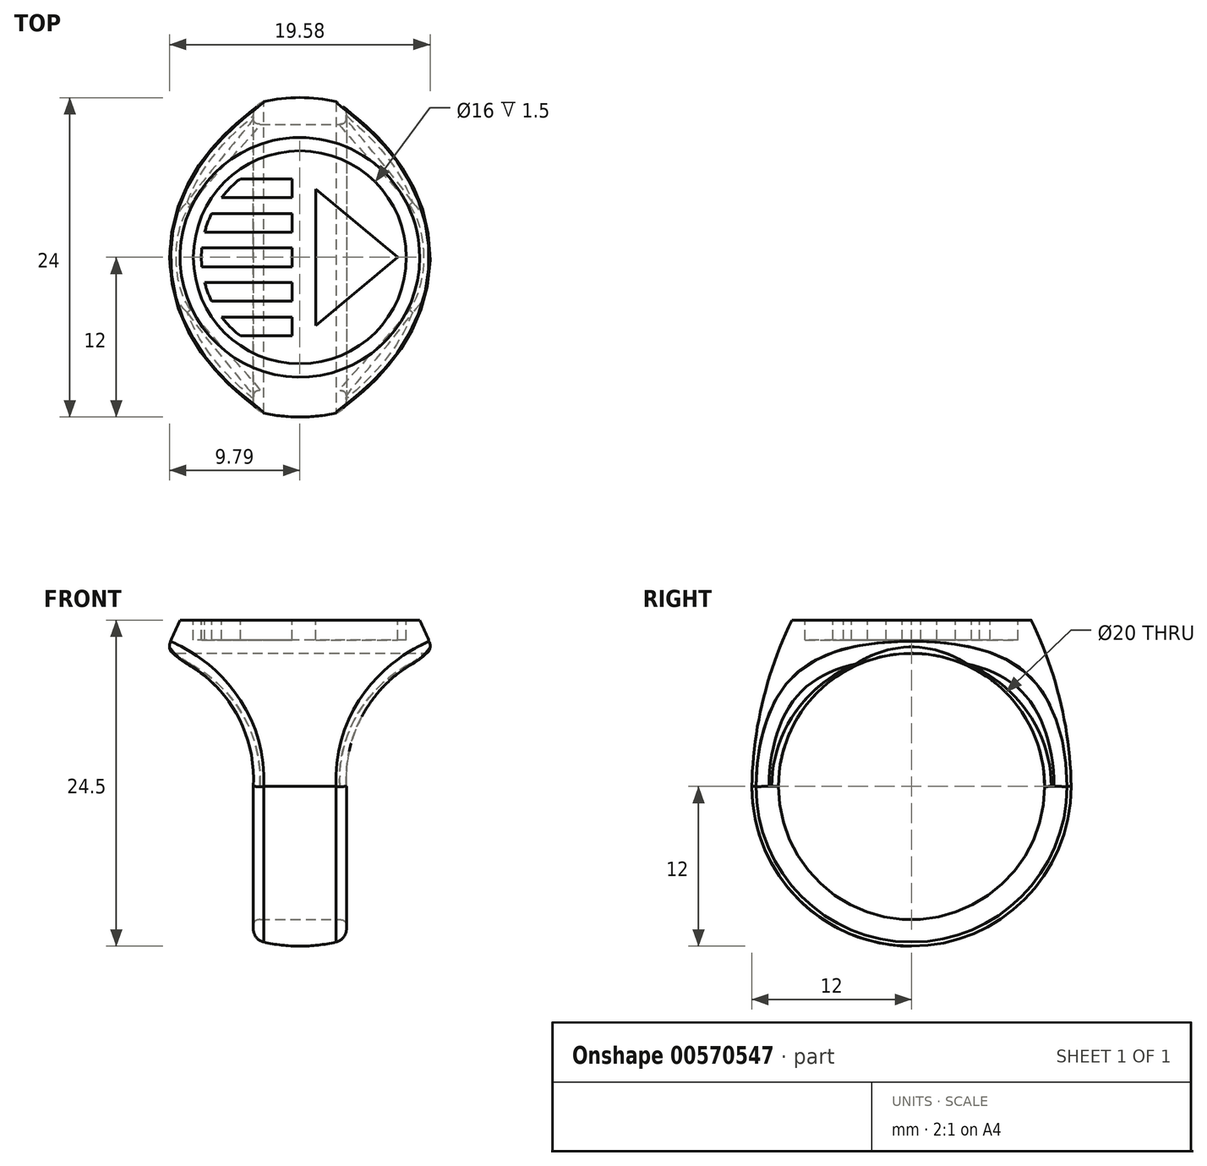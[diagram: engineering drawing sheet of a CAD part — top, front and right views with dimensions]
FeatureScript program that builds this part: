
annotation { "Feature Type Name" : "Feature", "Feature Type Description" : "" }
export const myFeature = defineFeature(function(context is Context, id is Id, definition is map)
    precondition{}
    {
        {
            var Q0;
            Q0=qCreatedBy(makeId("Right.planeOp"),FACE);
            var sketch = newSketch(context, id + "F0", { "sketchPlane" : qUnion([Q0])});
            skLineSegment(sketch, "E0", {"start": v(0, 0) * mm, "end": v(0, -24.5) * mm});
            skLineSegment(sketch, "E1", {"start": v(0, 0) * mm, "end": v(-9, 0) * mm});
            skArc(sketch, "E2", {"start": v(-12, -12.5) * mm, "mid": v(-8.49, -20.99) * mm, "end": v(0, -24.5) * mm});
            skLineSegment(sketch, "E3", {"start": v(0, -12.5) * mm, "end": v(-12, -12.5) * mm, "construction": true});
            skArc(sketch, "E4", {"start": v(-9, 0) * mm, "mid": v(-11.18, -6.09) * mm, "end": v(-12, -12.5) * mm});
            skSolve(sketch);
        }
        {
            var Q0;
            Q0=makeQuery(id+"F0.imprint","IMPRINT",FACE,{"disambiguationData":[TD([[makeQuery(id+"F0.imprint","IMPRINT",EDGE,{"derivedFrom":sQuery(id+"F0.wireOp",EDGE,"E0")}),-1.0]])]});
            var Q1;
            Q1=sQuery(id+"F0.wireOp",EDGE,"E0");
            revolve(context, id + "F1", {"entities" : qUnion([Q0]), "axis" : qUnion([Q1]), "revolveType" : RevolveType.FULL});
        }
        {
            var Q0;
            Q0=qCreatedBy(makeId("Right.planeOp"),FACE);
            var sketch = newSketch(context, id + "F2", { "sketchPlane" : qUnion([Q0])});
            skCircle(sketch, "E5", {"center": v(0, -12.5) * mm, "radius": 10 * mm});
            skSolve(sketch);
        }
        {
            var Q0;
            Q0=qSketchRegion(id+"F2",true);
            extrude(context, id + "F3", {"entities" : qUnion([Q0]), "operationType" : NewBodyOperationType.REMOVE, "oppositeDirection" : true, "depth" : 25 * mm, "offsetDistance" : 25 * mm, "symmetric" : true});
        }
        {
            var Q0;
            Q0=qCreatedBy(makeId("Front.planeOp"),FACE);
            var sketch = newSketch(context, id + "F4", { "sketchPlane" : qUnion([Q0])});
            skLineSegment(sketch, "E6", {"start": v(3.5, -26.5) * mm, "end": v(3.5, -12.5) * mm});
            skArc(sketch, "E7", {"start": v(10.15, -2.5) * mm, "mid": v(5.16, -6.39) * mm, "end": v(3.5, -12.5) * mm});
            skLineSegment(sketch, "E8", {"start": v(10.15, -2.5) * mm, "end": v(11.65, -2.5) * mm});
            skLineSegment(sketch, "E9", {"start": v(11.65, -2.5) * mm, "end": v(11.65, -26.5) * mm});
            skLineSegment(sketch, "E10", {"start": v(11.65, -26.5) * mm, "end": v(3.5, -26.5) * mm});
            skPoint(sketch, "E11.start.orphan", {"position": v(0, -24.5) * mm});
            skLineSegment(sketch, "E12", {"start": v(0, 0) * mm, "end": v(0, -24.5) * mm, "construction": true});
            skLineSegment(sketch, "E13.MirrorCS", {"start": v(-3.5, -26.5) * mm, "end": v(-3.5, -12.5) * mm});
            skArc(sketch, "E14.MirrorCS", {"start": v(-10.15, -2.5) * mm, "mid": v(-5.16, -6.39) * mm, "end": v(-3.5, -12.5) * mm});
            skLineSegment(sketch, "E15.MirrorCS", {"start": v(-11.65, -2.5) * mm, "end": v(-11.65, -26.5) * mm});
            skLineSegment(sketch, "E16.MirrorCS", {"start": v(-11.65, -26.5) * mm, "end": v(-3.5, -26.5) * mm});
            skLineSegment(sketch, "E17.MirrorCS", {"start": v(-10.15, -2.5) * mm, "end": v(-11.65, -2.5) * mm});
            skSolve(sketch);
        }
        {
            var Q0;
            Q0=qSketchRegion(id+"F4",true);
            extrude(context, id + "F5", {"entities" : qUnion([Q0]), "operationType" : NewBodyOperationType.REMOVE, "depth" : 25 * mm, "offsetDistance" : 25 * mm, "symmetric" : true});
        }
        {
            var Q0;
            Q0=makeQuery(id+"F1.opRevolve","SWEPT_FACE",FACE,{"disambiguationData":[OSD([sQuery(id+"F0.wireOp",EDGE,"E1")])]});
            var sketch = newSketch(context, id + "F6", { "sketchPlane" : qUnion([Q0])});
            skCircle(sketch, "E18", {"center": v(0, 0) * mm, "radius": 8 * mm});
            skLineSegment(sketch, "E19", {"start": v(-8, 0) * mm, "end": v(8, 0) * mm, "construction": true});
            skLineSegment(sketch, "E20", {"start": v(0, 7.69) * mm, "end": v(7.93, 1.07) * mm});
            skLineSegment(sketch, "E21", {"start": v(1.2, 0) * mm, "end": v(1.2, 5.13) * mm});
            skLineSegment(sketch, "E22", {"start": v(1.2, 5.13) * mm, "end": v(7.34, 0) * mm});
            skLineSegment(sketch, "E23", {"start": v(0, 7.69) * mm, "end": v(0, 0) * mm});
            skArc(sketch, "E24.trimOffspring", {"start": v(-4.47, 5.9) * mm, "mid": v(-5.22, 5.25) * mm, "end": v(-5.88, 4.5) * mm});
            skLineSegment(sketch, "E25", {"start": v(-7.37, 0.7) * mm, "end": v(-0.6, 0.7) * mm});
            skLineSegment(sketch, "E26", {"start": v(-0.6, 0.7) * mm, "end": v(-0.6, 0) * mm});
            skLineSegment(sketch, "E27", {"start": v(-7.15, 1.9) * mm, "end": v(-0.6, 1.9) * mm});
            skLineSegment(sketch, "E28", {"start": v(-0.6, 1.9) * mm, "end": v(-0.6, 3.3) * mm});
            skLineSegment(sketch, "E29", {"start": v(-0.6, 3.3) * mm, "end": v(-6.62, 3.3) * mm});
            skLineSegment(sketch, "E30", {"start": v(-5.88, 4.5) * mm, "end": v(-0.6, 4.5) * mm});
            skLineSegment(sketch, "E31", {"start": v(-0.6, 4.5) * mm, "end": v(-0.6, 5.9) * mm});
            skLineSegment(sketch, "E32", {"start": v(-0.6, 5.9) * mm, "end": v(-4.47, 5.9) * mm});
            skArc(sketch, "E33.trimOffspring", {"start": v(-7.37, 0.7) * mm, "mid": v(-7.4, 0.35) * mm, "end": v(-7.4, 0) * mm});
            skArc(sketch, "E34.trimOffspring", {"start": v(-6.62, 3.3) * mm, "mid": v(-6.92, 2.61) * mm, "end": v(-7.15, 1.9) * mm});
            skPoint(sketch, "E35.orphan", {"position": v(-0.6, 7.38) * mm});
            skLineSegment(sketch, "E36.MirrorCS", {"start": v(1.2, -5.13) * mm, "end": v(7.34, 0) * mm});
            skLineSegment(sketch, "E37.MirrorCS", {"start": v(0, -7.69) * mm, "end": v(7.93, -1.07) * mm});
            skLineSegment(sketch, "E38.MirrorCS", {"start": v(1.2, 0) * mm, "end": v(1.2, -5.13) * mm});
            skLineSegment(sketch, "E39.MirrorCS", {"start": v(0, -7.69) * mm, "end": v(0, 0) * mm});
            skLineSegment(sketch, "E40.MirrorCS", {"start": v(-5.88, -4.5) * mm, "end": v(-0.6, -4.5) * mm});
            skLineSegment(sketch, "E41.MirrorCS", {"start": v(-0.6, -5.9) * mm, "end": v(-4.47, -5.9) * mm});
            skArc(sketch, "E42.MirrorCS", {"start": v(-4.47, -5.9) * mm, "mid": v(-5.22, -5.25) * mm, "end": v(-5.88, -4.5) * mm});
            skLineSegment(sketch, "E43.MirrorCS", {"start": v(-0.6, -3.3) * mm, "end": v(-6.62, -3.3) * mm});
            skLineSegment(sketch, "E44.MirrorCS", {"start": v(-7.15, -1.9) * mm, "end": v(-0.6, -1.9) * mm});
            skArc(sketch, "E45.MirrorCS", {"start": v(-6.62, -3.3) * mm, "mid": v(-6.92, -2.61) * mm, "end": v(-7.15, -1.9) * mm});
            skLineSegment(sketch, "E46.MirrorCS", {"start": v(-7.37, -0.7) * mm, "end": v(-0.6, -0.7) * mm});
            skArc(sketch, "E47.MirrorCS", {"start": v(-7.37, -0.7) * mm, "mid": v(-7.4, -0.35) * mm, "end": v(-7.4, 0) * mm});
            skLineSegment(sketch, "E48", {"start": v(-0.6, -5.9) * mm, "end": v(-0.6, -4.5) * mm});
            skLineSegment(sketch, "E49", {"start": v(-0.6, -3.3) * mm, "end": v(-0.6, -1.9) * mm});
            skLineSegment(sketch, "E50", {"start": v(-0.6, -0.7) * mm, "end": v(-0.6, 0) * mm});
            skSolve(sketch);
        }
        {
            var Q0;
            Q0=qSketchRegion(id+"F6",true);
            var Q1;
            Q1=makeQuery(id+"F6.imprint","IMPRINT",FACE,{"disambiguationData":[TD([[makeQuery(id+"F6.imprint","IMPRINT",EDGE,{"derivedFrom":sQuery(id+"F6.wireOp",EDGE,"g20j87Mm-wGr7-AMiz-bI8b-qS7GuHKO57cL")}),1.0]])]});
            extrude(context, id + "F7", {"entities" : qUnion([Q0, Q1]), "operationType" : NewBodyOperationType.REMOVE, "oppositeDirection" : true, "depth" : 1.5 * mm, "offsetDistance" : 25 * mm});
        }
        {
            var Q0;
            Q0=makeQuery(id+"F5.boolean.opBoolean","INTERSECT",EDGE,{"disambiguationData":[OD(1.0)],"derivedFrom":[makeQuery(id+"F1.opRevolve","SWEPT_FACE",FACE,{"disambiguationData":[OSD([sQuery(id+"F0.wireOp",EDGE,"E4")])]}),makeQuery(id+"F5.opExtrude","SWEPT_FACE",FACE,{"disambiguationData":[OSD([sQuery(id+"F4.wireOp",EDGE,"E14.MirrorCS")])]})]});
            var Q1;
            Q1=makeQuery(id+"F5.boolean.opBoolean","INTERSECT",EDGE,{"derivedFrom":[makeQuery(id+"F1.opRevolve","SWEPT_FACE",FACE,{"disambiguationData":[OSD([sQuery(id+"F0.wireOp",EDGE,"E2")])]}),makeQuery(id+"F5.opExtrude","SWEPT_FACE",FACE,{"disambiguationData":[OSD([sQuery(id+"F4.wireOp",EDGE,"E13.MirrorCS")])]})]});
            var Q2;
            Q2=makeQuery(id+"F5.boolean.opBoolean","INTERSECT",EDGE,{"disambiguationData":[OD(1.0)],"derivedFrom":[makeQuery(id+"F1.opRevolve","SWEPT_FACE",FACE,{"disambiguationData":[OSD([sQuery(id+"F0.wireOp",EDGE,"E4")])]}),makeQuery(id+"F5.opExtrude","SWEPT_FACE",FACE,{"disambiguationData":[OSD([sQuery(id+"F4.wireOp",EDGE,"E7")])]})]});
            var Q3;
            Q3=makeQuery(id+"F5.boolean.opBoolean","INTERSECT",EDGE,{"derivedFrom":[makeQuery(id+"F1.opRevolve","SWEPT_FACE",FACE,{"disambiguationData":[OSD([sQuery(id+"F0.wireOp",EDGE,"E2")])]}),makeQuery(id+"F5.opExtrude","SWEPT_FACE",FACE,{"disambiguationData":[OSD([sQuery(id+"F4.wireOp",EDGE,"E6")])]})]});
            fillet(context, id + "F8", {"entities" : qUnion([Q0, Q1, Q2, Q3]), "radius" : 1 * mm, "allowEdgeOverflow" : false});
        }
        {
            var Q0;
            Q0=makeQuery(id+"F5.boolean.opBoolean","INTERSECT",EDGE,{"disambiguationData":[OD(1.0)],"derivedFrom":[makeQuery(id+"F3.boolean.opBoolean","COPY",FACE,{"derivedFrom":makeQuery(id+"F3.opExtrude","SWEPT_FACE",FACE,{"disambiguationData":[OSD([sQuery(id+"F2.wireOp",EDGE,"E5")])]})}),makeQuery(id+"F5.opExtrude","SWEPT_FACE",FACE,{"disambiguationData":[OSD([sQuery(id+"F4.wireOp",EDGE,"E14.MirrorCS")])]})]});
            var Q1;
            Q1=makeQuery(id+"F5.boolean.opBoolean","INTERSECT",EDGE,{"derivedFrom":[makeQuery(id+"F3.boolean.opBoolean","COPY",FACE,{"derivedFrom":makeQuery(id+"F3.opExtrude","SWEPT_FACE",FACE,{"disambiguationData":[OSD([sQuery(id+"F2.wireOp",EDGE,"E5")])]})}),makeQuery(id+"F5.opExtrude","SWEPT_FACE",FACE,{"disambiguationData":[OSD([sQuery(id+"F4.wireOp",EDGE,"E13.MirrorCS")])]})]});
            var Q2;
            Q2=makeQuery(id+"F5.boolean.opBoolean","INTERSECT",EDGE,{"disambiguationData":[OD(0.0)],"derivedFrom":[makeQuery(id+"F3.boolean.opBoolean","COPY",FACE,{"derivedFrom":makeQuery(id+"F3.opExtrude","SWEPT_FACE",FACE,{"disambiguationData":[OSD([sQuery(id+"F2.wireOp",EDGE,"E5")])]})}),makeQuery(id+"F5.opExtrude","SWEPT_FACE",FACE,{"disambiguationData":[OSD([sQuery(id+"F4.wireOp",EDGE,"E14.MirrorCS")])]})]});
            var Q3;
            Q3=makeQuery(id+"F5.boolean.opBoolean","INTERSECT",EDGE,{"disambiguationData":[OD(0.0)],"derivedFrom":[makeQuery(id+"F3.boolean.opBoolean","COPY",FACE,{"derivedFrom":makeQuery(id+"F3.opExtrude","SWEPT_FACE",FACE,{"disambiguationData":[OSD([sQuery(id+"F2.wireOp",EDGE,"E5")])]})}),makeQuery(id+"F5.opExtrude","SWEPT_FACE",FACE,{"disambiguationData":[OSD([sQuery(id+"F4.wireOp",EDGE,"E7")])]})]});
            var Q4;
            Q4=makeQuery(id+"F3.boolean.opBoolean","COPY",FACE,{"derivedFrom":makeQuery(id+"F3.opExtrude","SWEPT_FACE",FACE,{"disambiguationData":[OSD([sQuery(id+"F2.wireOp",EDGE,"E5")])]})});
            fillet(context, id + "F9", {"entities" : qUnion([Q0, Q1, Q2, Q3, Q4]), "radius" : .5 * mm, "rho" : 0.5, "crossSection" : FilletCrossSection.CONIC, "allowEdgeOverflow" : false});
        }
    });
